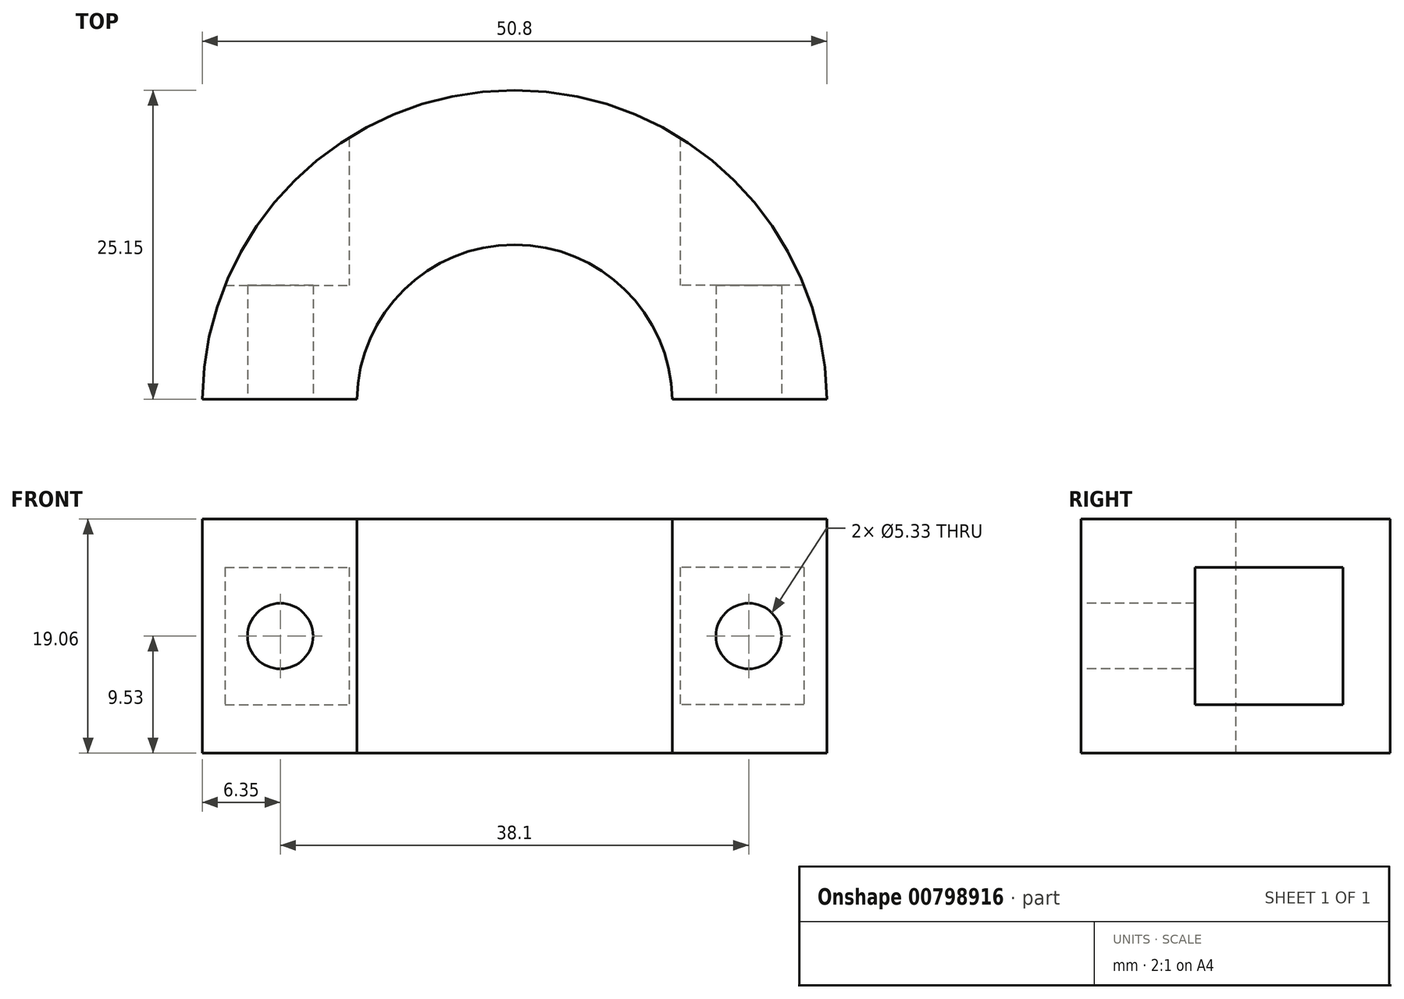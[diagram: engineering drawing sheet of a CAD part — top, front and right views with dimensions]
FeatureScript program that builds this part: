
annotation { "Feature Type Name" : "Feature", "Feature Type Description" : "" }
export const myFeature = defineFeature(function(context is Context, id is Id, definition is map)
    precondition{}
    {
        {
            var Q0;
            Q0=qCreatedBy(makeId("Top.planeOp"),FACE);
            var sketch = newSketch(context, id + "F0", { "sketchPlane" : qUnion([Q0])});
            skArc(sketch, "E0", {"start": v(12.82, 0.25) * mm, "mid": v(0, 12.83) * mm, "end": v(-12.82, 0.25) * mm});
            skArc(sketch, "E1", {"start": v(25.4, 0.25) * mm, "mid": v(0, 25.4) * mm, "end": v(-25.4, 0.25) * mm});
            skLineSegment(sketch, "E2", {"start": v(-25.4, 0.25) * mm, "end": v(-12.82, 0.25) * mm});
            skLineSegment(sketch, "E3.trimOffspring", {"start": v(12.82, 0.25) * mm, "end": v(25.4, 0.25) * mm});
            skSolve(sketch);
        }
        {
            var Q0;
            Q0=qSketchRegion(id+"F0",true);
            extrude(context, id + "F1", {"entities" : qUnion([Q0]), "endBound" : BoundingType.SYMMETRIC, "depth" : 19.05 * mm, "offsetDistance" : 25.4 * mm});
        }
        {
            var Q0;
            Q0=qCreatedBy(makeId("Front.planeOp"),FACE);
            var sketch = newSketch(context, id + "F2", { "sketchPlane" : qUnion([Q0])});
            skCircle(sketch, "E4", {"center": v(-19.05, 0) * mm, "radius": 2.67 * mm});
            skCircle(sketch, "E5", {"center": v(19.05, 0) * mm, "radius": 2.67 * mm});
            skSolve(sketch);
        }
        {
            var Q0;
            Q0=qCreatedBy(makeId("Front.planeOp"),FACE);
            cPlane(context, id + "F3", {"entities" : qUnion([Q0]), "cplaneType" : CPlaneType.OFFSET, "offset" : 9.52 * mm, "oppositeDirection" : true, "width" : 152.4 * mm, "height" : 152.4 * mm});
        }
        {
            var Q0;
            Q0=qSketchRegion(id+"F2",true);
            extrude(context, id + "F4", {"entities" : qUnion([Q0]), "operationType" : NewBodyOperationType.REMOVE, "endBound" : BoundingType.THROUGH_ALL, "oppositeDirection" : true, "depth" : 25.4 * mm, "offsetDistance" : 25.4 * mm});
        }
        {
            var Q0;
            Q0=qCreatedBy(id+"F3.planeOp",FACE);
            var sketch = newSketch(context, id + "F5", { "sketchPlane" : qUnion([Q0])});
            skCircle(sketch, "E6.0", {"center": v(19.05, 0) * mm, "radius": 2.67 * mm, "construction": true});
            skCircle(sketch, "E7.0", {"center": v(-19.05, 0) * mm, "radius": 2.67 * mm, "construction": true});
            skLineSegment(sketch, "E8.0", {"start": v(25.4, 9.53) * mm, "end": v(25.4, -9.52) * mm, "construction": true});
            skLineSegment(sketch, "E9.0", {"start": v(-25.4, 9.53) * mm, "end": v(-25.4, -9.52) * mm, "construction": true});
            skLineSegment(sketch, "E10", {"start": v(25.4, 0) * mm, "end": v(-25.4, 0) * mm, "construction": true});
            skLineSegment(sketch, "E11.bottom", {"start": v(25.4, 5.59) * mm, "end": v(13.46, 5.59) * mm});
            skLineSegment(sketch, "E11.top", {"start": v(25.4, -5.59) * mm, "end": v(13.46, -5.59) * mm});
            skLineSegment(sketch, "E11.left", {"start": v(25.4, 5.59) * mm, "end": v(25.4, -5.59) * mm});
            skLineSegment(sketch, "E11.right", {"start": v(13.46, 5.59) * mm, "end": v(13.46, -5.59) * mm});
            skLineSegment(sketch, "E12.bottom", {"start": v(-25.4, 5.59) * mm, "end": v(-13.46, 5.59) * mm});
            skLineSegment(sketch, "E12.top", {"start": v(-25.4, -5.59) * mm, "end": v(-13.46, -5.59) * mm});
            skLineSegment(sketch, "E12.left", {"start": v(-25.4, 5.59) * mm, "end": v(-25.4, -5.59) * mm});
            skLineSegment(sketch, "E12.right", {"start": v(-13.46, 5.59) * mm, "end": v(-13.46, -5.59) * mm});
            skSolve(sketch);
        }
        {
            var Q0;
            Q0=qSketchRegion(id+"F5",true);
            extrude(context, id + "F6", {"entities" : qUnion([Q0]), "operationType" : NewBodyOperationType.REMOVE, "endBound" : BoundingType.THROUGH_ALL, "oppositeDirection" : true, "depth" : 25.4 * mm, "offsetDistance" : 25.4 * mm});
        }
    });
